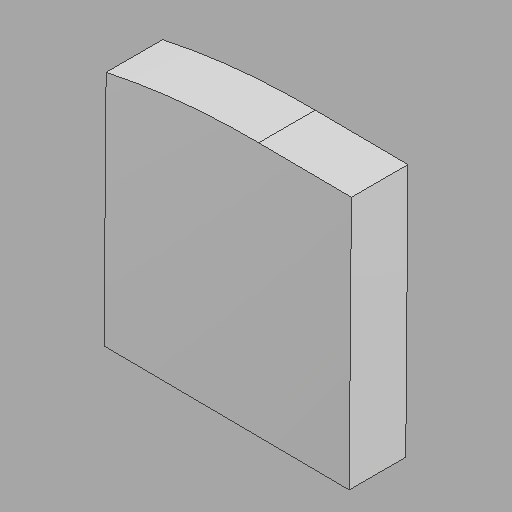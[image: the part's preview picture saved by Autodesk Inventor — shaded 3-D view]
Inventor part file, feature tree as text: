
AUTODESK INVENTOR PART (.ipt)
format: ipt  version: 2022.1 (Build 261234020, 234B)  size: 89,600 bytes
history: imported  units: in
note: dims shown in document units (in); Inventor stores cm internally (conversion verified against a paired STEP export)
features: imported_body x1
ambient origin geometry x8: Origin, YZ Plane, XZ Plane, XY Plane, X Axis, Y Axis, Z Axis, Center Point
bodies: Solid1 (imported_parasolid)
feature tree (1):
  imported_body  NMx_Import_Brep_tag  [imported B-rep: ~7 faces, bbox_mm=[666.359512, 687.953551, 152.4]]
